# Revit family: Shower_Ceiling_Nero_II_250mm
name_source: partatom
category: Plumbing Fixtures
units: mm (PartAtom-declared; Revit-internal decimal feet)

## family parameters
Always vertical = Yes
Cut with Voids When Loaded = Yes
Maintain Annotation Orientation = No
OmniClass Number = 23.31.17.00
OmniClass Title = Showers
Part Type = Normal
Room Calculation Point = No
Round Connector Dimension = Use Diameter
Shared = No
Work Plane-Based = No

## types (5) — shared parameters
Assembly Code = D2010
CW Connection = Yes
Default Elevation = 1050 mm
HW Connection = Yes
Manufacturer = Nero
ManufacturerOverallDepth = 250 mm  [stored 0.82021 ft]
ManufacturerOverallHeight = 51 mm
ManufacturerOverallWidth = 250 mm  [stored 0.82021 ft]
ModifiedIssue = 20251105 $
URL = https://nerotapware.com.au
Uniclass2015Code = Pr_40_20_87
Uniclass2015Title = Taps and water supply outlet fittings
Vent Connection = No
Waste Connection = No
zero-valued in all types: CWFU, HWFU, WFU

## per-type parameters (varying)
| type | Description | ManufacturerSpecCode | Material | Model | Type Comments |
| Chrome (NR5070046CH) | 250mm Round Metal Shower Head II Chrome | NR5070046CH | Metal_Chrome_Nero | NR5070046CH | Shower - Ceiling - 250mm - Chrome |
| Matte Black (NR5070046MB) | 250mm Round Metal Shower Head II Matte Black | NR5070046MB | Metal_MatteBlack_Nero | NR5070046MB | Shower - Ceiling - 250mm - Matte Black |
| Brushed Nickel (NR5070046BN) | 250mm Round Metal Shower Head II Brushed Nickel | NR5070046BN | Metal_Nickel_Nero_Brushed | NR5070046BN | Shower - Ceiling - 250mm - Brushed Nickel |
| Brushed Gold (NR5070046BG) | 250mm Round Metal Shower Head II Brushed Gold | NR5070046BG | Metal_Gold_Nero_Brushed | NR5070046BG | Shower - Ceiling - 250mm - Brushed Gold |
| Gunmetal (NR5070046GM) | 250mm Round Metal Shower Head II Gun Metal | NR5070046GM | Metal_GunMetal_Nero | NR5070046GM | Shower - Ceiling - 250mm - Brushed Gold |

note: [stored X ft] marks values corroborated as IEEE doubles in the binary element streams (Revit-internal decimal feet)

## geometry (parser evidence)
native form markers: Sweep x2
no freeform markers — native parametric forms only
